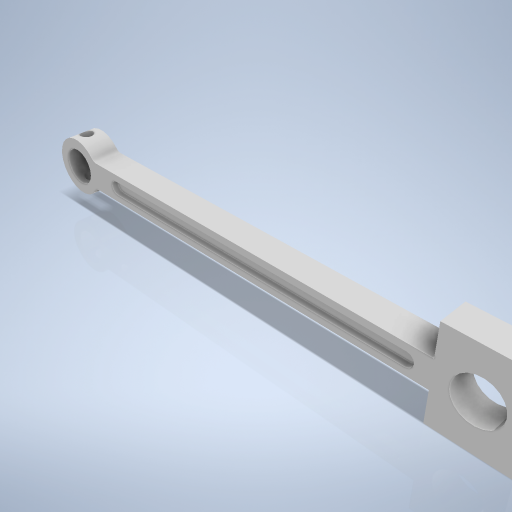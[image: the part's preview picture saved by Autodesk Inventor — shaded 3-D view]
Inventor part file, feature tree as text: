
AUTODESK INVENTOR PART (.ipt)
format: ipt  version: 2024.2 (Build 282272000, 272)  size: 340,480 bytes
history: native  units: mm
features: sketch x6, extrude x5, hole x3, plane x2, projected_geometry x2, fillet x1
ambient origin geometry x8: Origin, YZ Plane, XZ Plane, XY Plane, X Axis, Y Axis, Z Axis, Center Point
bodies: Volumenkörper1 (feature_tree)
feature tree (19):
  sketch  "Skizze1"  dims[d0=39.0mm d1=30.0mm]
  extrude  "Extrusion1"  Depth=30.0mm
  extrude  "Extrusion2"  Depth=12.0mm
  extrude  "Extrusion3"  Depth=6.0mm
  hole  "Bohrung1"  [1 undecoded]
  plane  "Arbeitsebene1"
  extrude  "Extrusion4"  Depth=3.0mm TaperAngle=0.0deg
  extrude  "Extrusion5"  TaperAngle=0.0deg  [1 undecoded]
  fillet  "Rundung1"  Radius=24.0mm
  plane  "Arbeitsebene2"
  hole  "Bohrung2"  [1 undecoded]
  hole  "Bohrung3"  [1 undecoded]
  sketch  "Skizze2"  dims[d2=184.4mm d3=12.0mm]
  sketch  "Skizze4"  dims[d4=6.0mm d5=6.0mm]
  sketch  "Skizze5"  dims[d6=3.0mm d8=12.0mm d9=0.0mm]
  sketch  "Skizze6"  dims[d10=3.0mm d11=0.0mm d12=3.0mm d13=0.0mm]
  projected_geometry  "Projizierte Kontur1"
  sketch  "Skizze7"  dims[d14=18.0mm d15=6.0mm d16=4.0mm d17=2.0mm d18=90.0deg d19=8.0mm d20=20.594885mm d23=0.0mm d24=24.0mm d25=12.0mm d26=0.0mm d27=142.0mm d28=15.0mm d29=12.0mm d30=0.0mm d31=3.0mm d32=12.0mm d34=6.0mm d35=6.0mm d36=4.0mm d37=2.0mm d38=90.0deg d39=8.0mm d40=20.594885mm d41=6.0mm d42=6.0mm d43=4.0mm d44=2.0mm d45=90.0deg d46=8.0mm d47=20.594885mm d48=6.0mm d50=13.5mm d51=13.5mm d33=0.5mm]
  projected_geometry  "Projizierte Kontur2"
note: 4 required parameter values undecoded (feature->parameter linkage not recoverable at this tier; creation-order binding heuristic only, values carry confidence <= 0.55)
